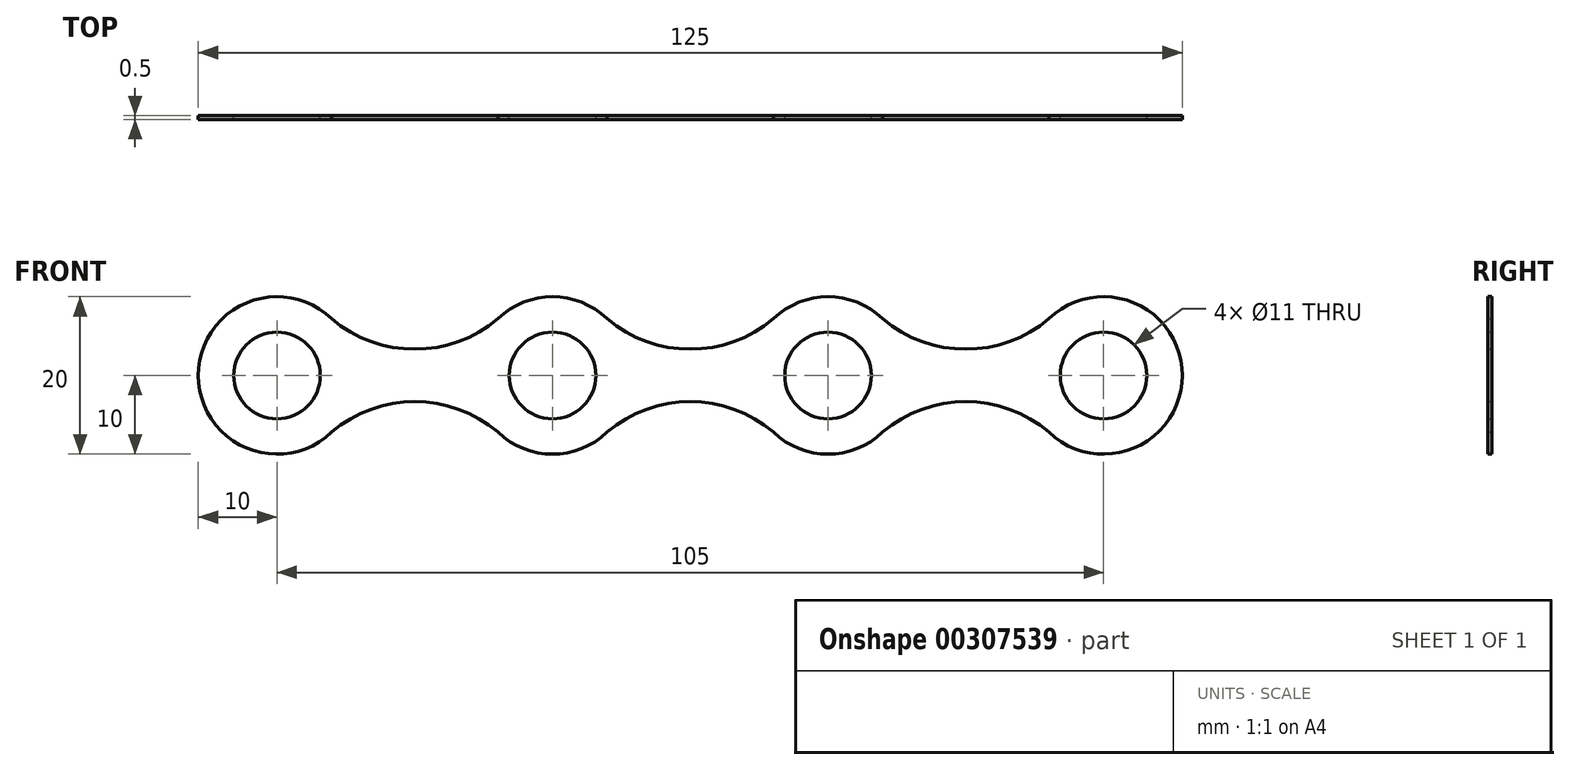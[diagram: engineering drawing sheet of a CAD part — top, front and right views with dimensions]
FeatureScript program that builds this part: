
annotation { "Feature Type Name" : "Feature", "Feature Type Description" : "" }
export const myFeature = defineFeature(function(context is Context, id is Id, definition is map)
    precondition{}
    {
        {
            var Q0;
            Q0=qCreatedBy(makeId("Front.planeOp"),FACE);
            cPlane(context, id + "F0", {"entities" : qUnion([Q0]), "cplaneType" : CPlaneType.OFFSET, "offset" : 1.5 * mm, "width" : 150 * mm, "height" : 150 * mm});
        }
        {
            var Q0;
            Q0=qCreatedBy(makeId("Front.planeOp"),FACE);
            var sketch = newSketch(context, id + "F1", { "sketchPlane" : qUnion([Q0])});
            skCircle(sketch, "E0", {"center": v(0, 0) * mm, "radius": 10 * mm});
            skSolve(sketch);
        }
        {
            var Q0;
            Q0=qCreatedBy(makeId("Front.planeOp"),FACE);
            var sketch = newSketch(context, id + "F2", { "sketchPlane" : qUnion([Q0])});
            skCircle(sketch, "E1", {"center": v(0, 0) * mm, "radius": 5.5 * mm});
            skSolve(sketch);
        }
        {
            var Q0;
            Q0=qSketchRegion(id+"F1",true);
            extrude(context, id + "F3", {"entities" : qUnion([Q0]), "depth" : 0.5 * mm, "offsetDistance" : 25 * mm});
        }
        {
            var Q0;
            Q0 = qSketchRegion(id + "F2", true);
            extrude(context, id + "F4", {"entities" : qUnion([Q0]), "operationType" : NewBodyOperationType.REMOVE, "depth" : 25 * mm, "offsetDistance" : 25 * mm});
        }
        {
            var Q0;
            Q0=makeQuery(id+"F3.opExtrude","SWEPT_BODY",BODY,{"disambiguationData":[OSD([sQuery(id+"F1.wireOp",EDGE,"E0")])]});
            transform(context, id + "F5", {"entities" : qUnion([Q0]), "transformType" : TransformType.TRANSLATION_3D, "dx" : 35 * mm, "dy" : 0 * mm, "dz" : 0 * mm, "makeCopy" : true});
        }
        {
            var Q0;
            Q0=makeQuery(id+"F3.opExtrude","SWEPT_BODY",BODY,{"disambiguationData":[OSD([sQuery(id+"F1.wireOp",EDGE,"E0")])]});
            transform(context, id + "F6", {"entities" : qUnion([Q0]), "transformType" : TransformType.TRANSLATION_3D, "dx" : 105 * mm, "dy" : 0 * mm, "dz" : 0 * mm, "makeCopy" : true});
        }
        {
            var Q0;
            Q0=makeQuery(id+"F3.opExtrude","SWEPT_BODY",BODY,{"disambiguationData":[OSD([sQuery(id+"F1.wireOp",EDGE,"E0")])]});
            transform(context, id + "F7", {"entities" : qUnion([Q0]), "transformType" : TransformType.TRANSLATION_3D, "dx" : 70 * mm, "dy" : 0 * mm, "dz" : 0 * mm, "makeCopy" : true});
        }
        {
            var Q0;
            Q0=qCreatedBy(makeId("Front.planeOp"),FACE);
            var sketch = newSketch(context, id + "F8", { "sketchPlane" : qUnion([Q0])});
            skArc(sketch, "E2", {"start": v(6.35, 7.73) * mm, "mid": v(17.5, 3.34) * mm, "end": v(28.65, 7.73) * mm});
            skArc(sketch, "E3.1.0.0", {"start": v(41.35, 7.73) * mm, "mid": v(52.5, 3.34) * mm, "end": v(63.65, 7.73) * mm});
            skArc(sketch, "E3.2.0.0", {"start": v(76.35, 7.73) * mm, "mid": v(87.5, 3.34) * mm, "end": v(98.65, 7.73) * mm});
            skLineSegment(sketch, "E3.direction1", {"start": v(6.35, 7.73) * mm, "end": v(41.35, 7.73) * mm, "construction": true});
            skArc(sketch, "E4.MirrorCS", {"start": v(76.35, -7.73) * mm, "mid": v(87.5, -3.34) * mm, "end": v(98.65, -7.73) * mm});
            skArc(sketch, "E5.MirrorCS", {"start": v(6.35, -7.73) * mm, "mid": v(17.5, -3.34) * mm, "end": v(28.65, -7.73) * mm});
            skArc(sketch, "E6.MirrorCS", {"start": v(41.35, -7.73) * mm, "mid": v(52.5, -3.34) * mm, "end": v(63.65, -7.73) * mm});
            skLineSegment(sketch, "E7", {"start": v(6.35, 7.73) * mm, "end": v(6.35, -7.73) * mm});
            skLineSegment(sketch, "E8", {"start": v(28.65, 7.73) * mm, "end": v(28.65, -7.73) * mm});
            skLineSegment(sketch, "E9", {"start": v(41.35, 7.73) * mm, "end": v(41.35, -7.73) * mm});
            skLineSegment(sketch, "E10", {"start": v(63.65, 7.73) * mm, "end": v(63.65, -7.73) * mm});
            skLineSegment(sketch, "E11", {"start": v(76.35, 7.73) * mm, "end": v(76.35, -7.73) * mm});
            skLineSegment(sketch, "E12", {"start": v(98.65, 7.73) * mm, "end": v(98.65, -7.73) * mm});
            skSolve(sketch);
        }
        {
            var Q0;
            Q0=makeQuery(id+"F8.imprint","IMPRINT",FACE,{"disambiguationData":[TD([[makeQuery(id+"F8.imprint","IMPRINT",EDGE,{"derivedFrom":sQuery(id+"F8.wireOp",EDGE,"E2")}),-1.0]])]});
            var Q1;
            Q1=makeQuery(id+"F8.imprint","IMPRINT",FACE,{"disambiguationData":[TD([[makeQuery(id+"F8.imprint","IMPRINT",EDGE,{"derivedFrom":sQuery(id+"F8.wireOp",EDGE,"E3.1.0.0")}),-1.0]])]});
            var Q2;
            Q2=makeQuery(id+"F8.imprint","IMPRINT",FACE,{"disambiguationData":[TD([[makeQuery(id+"F8.imprint","IMPRINT",EDGE,{"derivedFrom":sQuery(id+"F8.wireOp",EDGE,"E3.2.0.0")}),-1.0]])]});
            var Q3;
            Q3=sQuery(id+"F8.wireOp",EDGE,"E2");
            var Q4;
            Q4=sQuery(id+"F8.wireOp",EDGE,"E6.MirrorCS");
            var Q5;
            Q5=sQuery(id+"F8.wireOp",EDGE,"E5.MirrorCS");
            var Q6;
            Q6=sQuery(id+"F8.wireOp",EDGE,"E7");
            var Q7;
            Q7=sQuery(id+"F8.wireOp",EDGE,"E4.MirrorCS");
            var Q8;
            Q8=sQuery(id+"F8.wireOp",EDGE,"E3.1.0.0");
            var Q9;
            Q9=sQuery(id+"F8.wireOp",EDGE,"E8");
            var Q10;
            Q10=sQuery(id+"F8.wireOp",EDGE,"E3.2.0.0");
            var Q11;
            Q11=sQuery(id+"F8.wireOp",EDGE,"E9");
            var Q12;
            Q12=sQuery(id+"F8.wireOp",EDGE,"E10");
            var Q13;
            Q13=sQuery(id+"F8.wireOp",EDGE,"E11");
            var Q14;
            Q14=sQuery(id+"F8.wireOp",EDGE,"E12");
            extrude(context, id + "F9", {"entities" : qUnion([Q0, Q1, Q2]), "operationType" : NewBodyOperationType.ADD, "surfaceEntities" : qUnion([Q3, Q4, Q5, Q6, Q7, Q8, Q9, Q10, Q11, Q12, Q13, Q14]), "depth" : 0.5 * mm, "offsetDistance" : 25 * mm});
        }
    });
